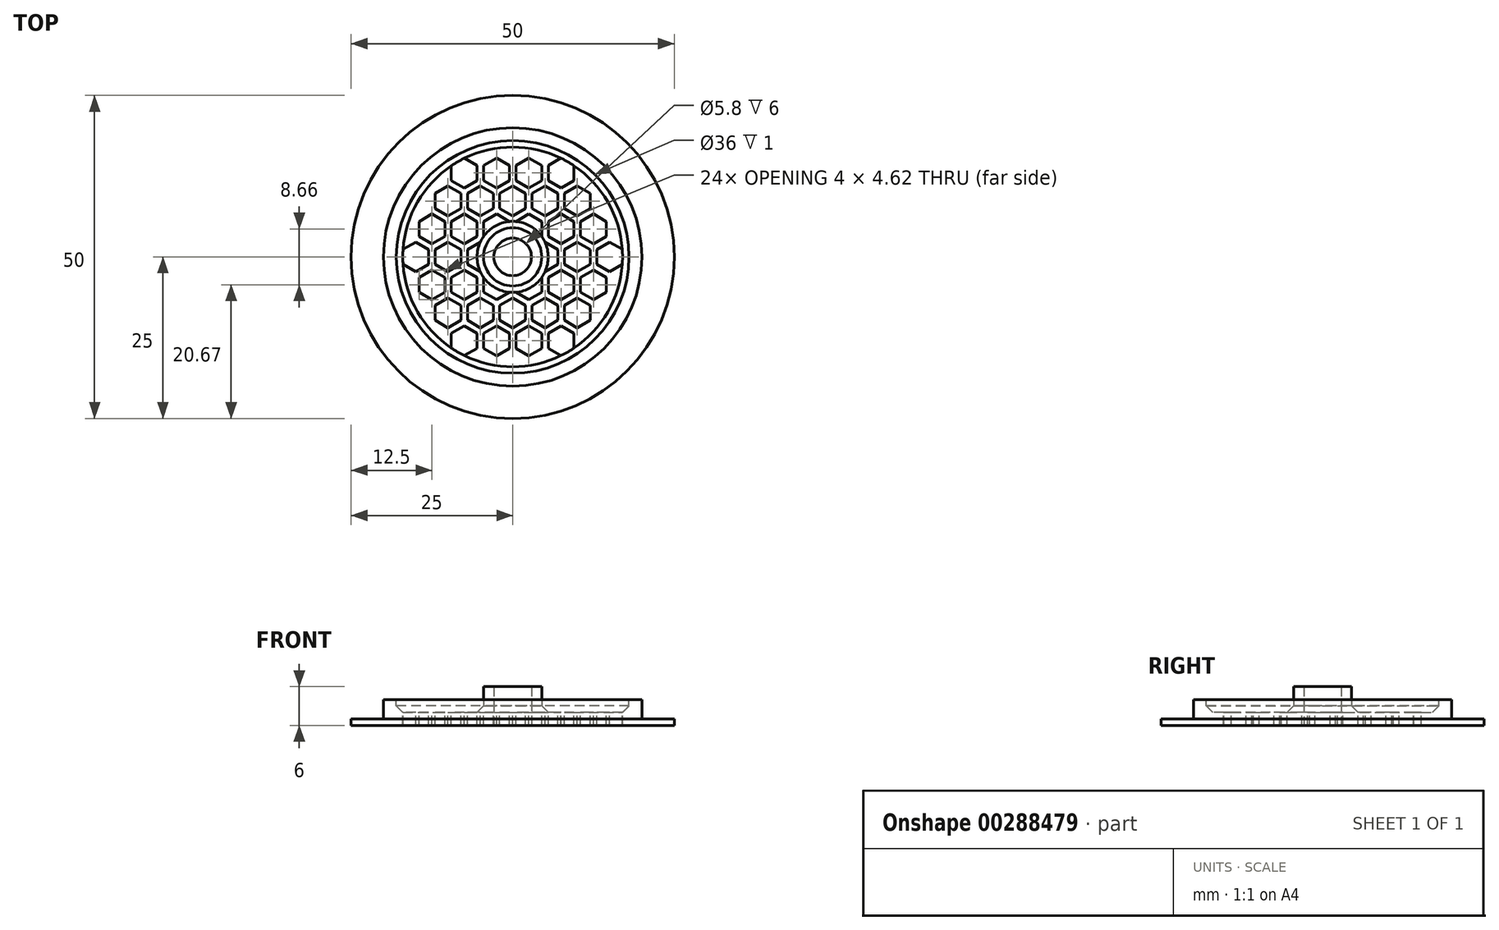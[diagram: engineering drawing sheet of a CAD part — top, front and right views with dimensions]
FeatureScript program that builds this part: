
annotation { "Feature Type Name" : "Feature", "Feature Type Description" : "" }
export const myFeature = defineFeature(function(context is Context, id is Id, definition is map)
    precondition{}
    {
        {
            var Q0;
            Q0=qCreatedBy(makeId("Top.planeOp"),FACE);
            var sketch = newSketch(context, id + "F0", { "sketchPlane" : qUnion([Q0])});
            skCircle(sketch, "E0", {"center": v(0, 0) * mm, "radius": 25 * mm});
            skCircle(sketch, "E1", {"center": v(0, 0) * mm, "radius": 20 * mm});
            skCircle(sketch, "E2", {"center": v(0, 0) * mm, "radius": 2.9 * mm});
            skSolve(sketch);
        }
        {
            var Q0;
            Q0=makeQuery(id+"F0.imprint","IMPRINT",FACE,{"disambiguationData":[TD([[makeQuery(id+"F0.imprint","IMPRINT",EDGE,{"derivedFrom":sQuery(id+"F0.wireOp",EDGE,"E1")}),1.0]])]});
            var Q1;
            Q1=makeQuery(id+"F0.imprint","IMPRINT",FACE,{"disambiguationData":[TD([[makeQuery(id+"F0.imprint","IMPRINT",EDGE,{"derivedFrom":sQuery(id+"F0.wireOp",EDGE,"E0")}),1.0]])]});
            extrude(context, id + "F1", {"entities" : qUnion([Q0, Q1]), "depth" : 1 * mm});
        }
        {
            var Q0;
            Q0=makeQuery(id+"F0.imprint","IMPRINT",FACE,{"disambiguationData":[TD([[makeQuery(id+"F0.imprint","IMPRINT",EDGE,{"derivedFrom":sQuery(id+"F0.wireOp",EDGE,"E1")}),1.0]])]});
            extrude(context, id + "F2", {"entities" : qUnion([Q0]), "operationType" : NewBodyOperationType.ADD, "depth" : 4 * mm});
        }
        {
            var Q0;
            Q0=makeQuery(id+"F2.opExtrude","CAP_FACE",FACE,{"disambiguationData":[OSD([sQuery(id+"F0.wireOp",EDGE,"E1"),sQuery(id+"F0.wireOp",EDGE,"E2")])],"isStart":false});
            var sketch = newSketch(context, id + "F3", { "sketchPlane" : qUnion([Q0])});
            skCircle(sketch, "E3", {"center": v(0, 0) * mm, "radius": 4.5 * mm});
            skCircle(sketch, "E4.0", {"center": v(0, 0) * mm, "radius": 18 * mm});
            skSolve(sketch);
        }
        {
            var Q0;
            Q0=makeQuery(id+"F3.imprint","IMPRINT",FACE,{"disambiguationData":[TD([[makeQuery(id+"F3.imprint","IMPRINT",EDGE,{"derivedFrom":sQuery(id+"F3.wireOp",EDGE,"E3")}),1.0]])]});
            extrude(context, id + "F4", {"entities" : qUnion([Q0]), "operationType" : NewBodyOperationType.ADD, "depth" : 2 * mm});
        }
        {
            var Q0;
            Q0=makeQuery(id+"F3.imprint","IMPRINT",FACE,{"disambiguationData":[TD([[makeQuery(id+"F3.imprint","IMPRINT",EDGE,{"derivedFrom":sQuery(id+"F3.wireOp",EDGE,"E3")}),-1.0]])]});
            extrude(context, id + "F5", {"entities" : qUnion([Q0]), "operationType" : NewBodyOperationType.REMOVE, "oppositeDirection" : true, "depth" : 2 * mm});
        }
        {
            var Q0;
            Q0=makeQuery(id+"F5.boolean.opBoolean","COPY",FACE,{"derivedFrom":makeQuery(id+"F5.opExtrude","CAP_FACE",FACE,{"disambiguationData":[OSD([sQuery(id+"F3.wireOp",EDGE,"E3"),sQuery(id+"F3.wireOp",EDGE,"E4.0")])],"isStart":false})});
            chamfer(context, id + "F6", {"entities" : qUnion([Q0]), "width" : 1 * mm, "tangentPropagation" : true});
        }
        {
            var Q0;
            Q0=makeQuery(id+"F5.boolean.opBoolean","COPY",FACE,{"derivedFrom":makeQuery(id+"F5.opExtrude","CAP_FACE",FACE,{"disambiguationData":[OSD([sQuery(id+"F3.wireOp",EDGE,"E3"),sQuery(id+"F3.wireOp",EDGE,"E4.0")])],"isStart":false})});
            var sketch = newSketch(context, id + "F7", { "sketchPlane" : qUnion([Q0])});
            skLineSegment(sketch, "E5.bottom", {"start": v(-17, 17) * mm, "end": v(17, 17) * mm, "construction": true});
            skLineSegment(sketch, "E5.top", {"start": v(-17, -17) * mm, "end": v(17, -17) * mm, "construction": true});
            skLineSegment(sketch, "E5.left", {"start": v(-17, 17) * mm, "end": v(-17, -17) * mm, "construction": true});
            skLineSegment(sketch, "E5.right", {"start": v(17, 17) * mm, "end": v(17, -17) * mm, "construction": true});
            skPoint(sketch, "E5.middle", {"position": v(0, 0) * mm});
            skCircle(sketch, "E6.cCircle", {"center": v(-2.5, -4.33) * mm, "radius": 2 * mm, "construction": true});
            skLineSegment(sketch, "E6.0", {"start": v(-0.5, -3.18) * mm, "end": v(-0.5, -5.48) * mm});
            skLineSegment(sketch, "E6.1", {"start": v(-0.5, -5.48) * mm, "end": v(-2.5, -6.64) * mm});
            skLineSegment(sketch, "E6.2", {"start": v(-2.5, -6.64) * mm, "end": v(-4.5, -5.48) * mm});
            skLineSegment(sketch, "E6.3", {"start": v(-4.5, -5.48) * mm, "end": v(-4.5, -3.18) * mm});
            skLineSegment(sketch, "E6.4", {"start": v(-4.5, -3.18) * mm, "end": v(-2.5, -2.02) * mm});
            skLineSegment(sketch, "E6.5", {"start": v(-2.5, -2.02) * mm, "end": v(-0.5, -3.18) * mm});
            skPoint(sketch, "E6.0.midPoint", {"position": v(-0.5, -4.33) * mm});
            skCircle(sketch, "E7.cCircle", {"center": v(-2.5, -4.33) * mm, "radius": 2.5 * mm, "construction": true});
            skLineSegment(sketch, "E7.0", {"start": v(0, -2.89) * mm, "end": v(0, -5.77) * mm, "construction": true});
            skLineSegment(sketch, "E7.1", {"start": v(0, -5.77) * mm, "end": v(-2.5, -7.22) * mm, "construction": true});
            skLineSegment(sketch, "E7.2", {"start": v(-2.5, -7.22) * mm, "end": v(-5, -5.77) * mm, "construction": true});
            skLineSegment(sketch, "E7.3", {"start": v(-5, -5.77) * mm, "end": v(-5, -2.89) * mm, "construction": true});
            skLineSegment(sketch, "E7.4", {"start": v(-5, -2.89) * mm, "end": v(-2.5, -1.44) * mm, "construction": true});
            skLineSegment(sketch, "E7.5", {"start": v(-2.5, -1.44) * mm, "end": v(0, -2.89) * mm, "construction": true});
            skPoint(sketch, "E7.0.midPoint", {"position": v(0, -4.33) * mm});
            skPoint(sketch, "E8.1.0", {"position": v(3.75, -2.17) * mm});
            skPoint(sketch, "E8.1.1", {"position": v(3.5, -2.6) * mm});
            skLineSegment(sketch, "E8.1.2", {"start": v(0, -2.89) * mm, "end": v(2.5, -1.44) * mm, "construction": true});
            skLineSegment(sketch, "E8.1.3", {"start": v(2.5, -1.44) * mm, "end": v(5, -2.89) * mm, "construction": true});
            skLineSegment(sketch, "E8.1.4", {"start": v(0.5, -3.18) * mm, "end": v(2.5, -2.02) * mm});
            skLineSegment(sketch, "E8.1.5", {"start": v(0.5, -5.48) * mm, "end": v(0.5, -3.18) * mm});
            skLineSegment(sketch, "E8.1.6", {"start": v(2.5, -6.64) * mm, "end": v(0.5, -5.48) * mm});
            skLineSegment(sketch, "E8.1.7", {"start": v(4.5, -5.48) * mm, "end": v(2.5, -6.64) * mm});
            skLineSegment(sketch, "E8.1.8", {"start": v(2.5, -7.22) * mm, "end": v(0, -5.77) * mm, "construction": true});
            skLineSegment(sketch, "E8.1.9", {"start": v(5, -5.77) * mm, "end": v(2.5, -7.22) * mm, "construction": true});
            skLineSegment(sketch, "E8.1.10", {"start": v(5, -2.89) * mm, "end": v(5, -5.77) * mm, "construction": true});
            skLineSegment(sketch, "E8.1.11", {"start": v(0, -5.77) * mm, "end": v(0, -2.89) * mm, "construction": true});
            skLineSegment(sketch, "E8.1.12", {"start": v(4.5, -3.18) * mm, "end": v(4.5, -5.48) * mm});
            skLineSegment(sketch, "E8.1.13", {"start": v(2.5, -2.02) * mm, "end": v(4.5, -3.18) * mm});
            skPoint(sketch, "E8.2.0", {"position": v(3.75, 2.17) * mm});
            skPoint(sketch, "E8.2.1", {"position": v(4, 1.73) * mm});
            skLineSegment(sketch, "E8.2.2", {"start": v(2.5, -1.44) * mm, "end": v(2.5, 1.44) * mm, "construction": true});
            skLineSegment(sketch, "E8.2.3", {"start": v(2.5, 1.44) * mm, "end": v(5, 2.89) * mm, "construction": true});
            skLineSegment(sketch, "E8.2.4", {"start": v(3, -1.15) * mm, "end": v(3, 1.15) * mm});
            skLineSegment(sketch, "E8.2.5", {"start": v(5, -2.3) * mm, "end": v(3, -1.15) * mm});
            skLineSegment(sketch, "E8.2.6", {"start": v(7, -1.15) * mm, "end": v(5, -2.3) * mm});
            skLineSegment(sketch, "E8.2.7", {"start": v(7, 1.15) * mm, "end": v(7, -1.15) * mm});
            skLineSegment(sketch, "E8.2.8", {"start": v(7.5, -1.44) * mm, "end": v(5, -2.89) * mm, "construction": true});
            skLineSegment(sketch, "E8.2.9", {"start": v(7.5, 1.44) * mm, "end": v(7.5, -1.44) * mm, "construction": true});
            skLineSegment(sketch, "E8.2.10", {"start": v(5, 2.89) * mm, "end": v(7.5, 1.44) * mm, "construction": true});
            skLineSegment(sketch, "E8.2.11", {"start": v(5, -2.89) * mm, "end": v(2.5, -1.44) * mm, "construction": true});
            skLineSegment(sketch, "E8.2.12", {"start": v(5, 2.3) * mm, "end": v(7, 1.15) * mm});
            skLineSegment(sketch, "E8.2.13", {"start": v(3, 1.15) * mm, "end": v(5, 2.3) * mm});
            skPoint(sketch, "E8.3.0", {"position": v(0, 4.33) * mm});
            skPoint(sketch, "E8.3.1", {"position": v(0.5, 4.33) * mm});
            skLineSegment(sketch, "E8.3.2", {"start": v(2.5, 1.44) * mm, "end": v(0, 2.89) * mm, "construction": true});
            skLineSegment(sketch, "E8.3.3", {"start": v(0, 2.89) * mm, "end": v(0, 5.77) * mm, "construction": true});
            skLineSegment(sketch, "E8.3.4", {"start": v(2.5, 2.02) * mm, "end": v(0.5, 3.18) * mm});
            skLineSegment(sketch, "E8.3.5", {"start": v(4.5, 3.18) * mm, "end": v(2.5, 2.02) * mm});
            skLineSegment(sketch, "E8.3.6", {"start": v(4.5, 5.48) * mm, "end": v(4.5, 3.18) * mm});
            skLineSegment(sketch, "E8.3.7", {"start": v(2.5, 6.64) * mm, "end": v(4.5, 5.48) * mm});
            skLineSegment(sketch, "E8.3.8", {"start": v(5, 5.77) * mm, "end": v(5, 2.89) * mm, "construction": true});
            skLineSegment(sketch, "E8.3.9", {"start": v(2.5, 7.22) * mm, "end": v(5, 5.77) * mm, "construction": true});
            skLineSegment(sketch, "E8.3.10", {"start": v(0, 5.77) * mm, "end": v(2.5, 7.22) * mm, "construction": true});
            skLineSegment(sketch, "E8.3.11", {"start": v(5, 2.89) * mm, "end": v(2.5, 1.44) * mm, "construction": true});
            skLineSegment(sketch, "E8.3.12", {"start": v(0.5, 5.48) * mm, "end": v(2.5, 6.64) * mm});
            skLineSegment(sketch, "E8.3.13", {"start": v(0.5, 3.18) * mm, "end": v(0.5, 5.48) * mm});
            skPoint(sketch, "E8.4.0", {"position": v(-3.75, 2.17) * mm});
            skPoint(sketch, "E8.4.1", {"position": v(-3.5, 2.6) * mm});
            skLineSegment(sketch, "E8.4.2", {"start": v(0, 2.89) * mm, "end": v(-2.5, 1.44) * mm, "construction": true});
            skLineSegment(sketch, "E8.4.3", {"start": v(-2.5, 1.44) * mm, "end": v(-5, 2.89) * mm, "construction": true});
            skLineSegment(sketch, "E8.4.4", {"start": v(-0.5, 3.18) * mm, "end": v(-2.5, 2.02) * mm});
            skLineSegment(sketch, "E8.4.5", {"start": v(-0.5, 5.48) * mm, "end": v(-0.5, 3.18) * mm});
            skLineSegment(sketch, "E8.4.6", {"start": v(-2.5, 6.64) * mm, "end": v(-0.5, 5.48) * mm});
            skLineSegment(sketch, "E8.4.7", {"start": v(-4.5, 5.48) * mm, "end": v(-2.5, 6.64) * mm});
            skLineSegment(sketch, "E8.4.8", {"start": v(-2.5, 7.22) * mm, "end": v(0, 5.77) * mm, "construction": true});
            skLineSegment(sketch, "E8.4.9", {"start": v(-5, 5.77) * mm, "end": v(-2.5, 7.22) * mm, "construction": true});
            skLineSegment(sketch, "E8.4.10", {"start": v(-5, 2.89) * mm, "end": v(-5, 5.77) * mm, "construction": true});
            skLineSegment(sketch, "E8.4.11", {"start": v(0, 5.77) * mm, "end": v(0, 2.89) * mm, "construction": true});
            skLineSegment(sketch, "E8.4.12", {"start": v(-4.5, 3.18) * mm, "end": v(-4.5, 5.48) * mm});
            skLineSegment(sketch, "E8.4.13", {"start": v(-2.5, 2.02) * mm, "end": v(-4.5, 3.18) * mm});
            skPoint(sketch, "E8.5.0", {"position": v(-3.75, -2.17) * mm});
            skPoint(sketch, "E8.5.1", {"position": v(-4, -1.73) * mm});
            skLineSegment(sketch, "E8.5.2", {"start": v(-2.5, 1.44) * mm, "end": v(-2.5, -1.44) * mm, "construction": true});
            skLineSegment(sketch, "E8.5.3", {"start": v(-2.5, -1.44) * mm, "end": v(-5, -2.89) * mm, "construction": true});
            skLineSegment(sketch, "E8.5.4", {"start": v(-3, 1.15) * mm, "end": v(-3, -1.15) * mm});
            skLineSegment(sketch, "E8.5.5", {"start": v(-5, 2.3) * mm, "end": v(-3, 1.15) * mm});
            skLineSegment(sketch, "E8.5.6", {"start": v(-7, 1.15) * mm, "end": v(-5, 2.3) * mm});
            skLineSegment(sketch, "E8.5.7", {"start": v(-7, -1.15) * mm, "end": v(-7, 1.15) * mm});
            skLineSegment(sketch, "E8.5.8", {"start": v(-7.5, 1.44) * mm, "end": v(-5, 2.89) * mm, "construction": true});
            skLineSegment(sketch, "E8.5.9", {"start": v(-7.5, -1.44) * mm, "end": v(-7.5, 1.44) * mm, "construction": true});
            skLineSegment(sketch, "E8.5.10", {"start": v(-5, -2.89) * mm, "end": v(-7.5, -1.44) * mm, "construction": true});
            skLineSegment(sketch, "E8.5.11", {"start": v(-5, 2.89) * mm, "end": v(-2.5, 1.44) * mm, "construction": true});
            skLineSegment(sketch, "E8.5.12", {"start": v(-5, -2.3) * mm, "end": v(-7, -1.15) * mm});
            skLineSegment(sketch, "E8.5.13", {"start": v(-3, -1.15) * mm, "end": v(-5, -2.3) * mm});
            skLineSegment(sketch, "E9", {"start": v(-2.5, -1.44) * mm, "end": v(0, 0) * mm, "construction": true});
            skLineSegment(sketch, "E10", {"start": v(0, 0) * mm, "end": v(0, -2.89) * mm, "construction": true});
            skLineSegment(sketch, "E11.MirrorCS", {"start": v(-2, 1.15) * mm, "end": v(-2, -1.15) * mm});
            skLineSegment(sketch, "E12.MirrorCS", {"start": v(-2, -1.15) * mm, "end": v(0, -2.3) * mm});
            skLineSegment(sketch, "E13.MirrorCS", {"start": v(0, -2.3) * mm, "end": v(2, -1.15) * mm});
            skLineSegment(sketch, "E14.MirrorCS", {"start": v(2, -1.15) * mm, "end": v(2, 1.15) * mm});
            skLineSegment(sketch, "E15.MirrorCS", {"start": v(2, 1.15) * mm, "end": v(0, 2.3) * mm});
            skLineSegment(sketch, "E16.MirrorCS", {"start": v(0, 2.3) * mm, "end": v(-2, 1.15) * mm});
            skLineSegment(sketch, "E17.MirrorCS", {"start": v(2, -7.5) * mm, "end": v(0, -6.35) * mm});
            skLineSegment(sketch, "E18.MirrorCS", {"start": v(0, -6.35) * mm, "end": v(-2, -7.5) * mm});
            skLineSegment(sketch, "E19.MirrorCS", {"start": v(-2, -7.5) * mm, "end": v(-2, -9.81) * mm});
            skLineSegment(sketch, "E20.MirrorCS", {"start": v(-2, -9.81) * mm, "end": v(0, -10.97) * mm});
            skLineSegment(sketch, "E21.MirrorCS", {"start": v(0, -10.97) * mm, "end": v(2, -9.81) * mm});
            skLineSegment(sketch, "E22.MirrorCS", {"start": v(2, -9.81) * mm, "end": v(2, -7.5) * mm});
            skLineSegment(sketch, "E23.1.0", {"start": v(5.5, -3.18) * mm, "end": v(5.5, -5.48) * mm});
            skLineSegment(sketch, "E23.1.1", {"start": v(5.5, -5.48) * mm, "end": v(7.5, -6.64) * mm});
            skLineSegment(sketch, "E23.1.2", {"start": v(7.5, -6.64) * mm, "end": v(9.5, -5.48) * mm});
            skLineSegment(sketch, "E23.1.3", {"start": v(9.5, -5.48) * mm, "end": v(9.5, -3.18) * mm});
            skLineSegment(sketch, "E23.1.4", {"start": v(9.5, -3.18) * mm, "end": v(7.5, -2.02) * mm});
            skLineSegment(sketch, "E23.1.5", {"start": v(7.5, -2.02) * mm, "end": v(5.5, -3.18) * mm});
            skLineSegment(sketch, "E23.2.0", {"start": v(5.5, 3.18) * mm, "end": v(7.5, 2.02) * mm});
            skLineSegment(sketch, "E23.2.1", {"start": v(7.5, 2.02) * mm, "end": v(9.5, 3.18) * mm});
            skLineSegment(sketch, "E23.2.2", {"start": v(9.5, 3.18) * mm, "end": v(9.5, 5.48) * mm});
            skLineSegment(sketch, "E23.2.3", {"start": v(9.5, 5.48) * mm, "end": v(7.5, 6.64) * mm});
            skLineSegment(sketch, "E23.2.4", {"start": v(7.5, 6.64) * mm, "end": v(5.5, 5.48) * mm});
            skLineSegment(sketch, "E23.2.5", {"start": v(5.5, 5.48) * mm, "end": v(5.5, 3.18) * mm});
            skLineSegment(sketch, "E23.3.0", {"start": v(0, 6.35) * mm, "end": v(2, 7.5) * mm});
            skLineSegment(sketch, "E23.3.1", {"start": v(2, 7.5) * mm, "end": v(2, 9.81) * mm});
            skLineSegment(sketch, "E23.3.2", {"start": v(2, 9.81) * mm, "end": v(0, 10.97) * mm});
            skLineSegment(sketch, "E23.3.3", {"start": v(0, 10.97) * mm, "end": v(-2, 9.81) * mm});
            skLineSegment(sketch, "E23.3.4", {"start": v(-2, 9.81) * mm, "end": v(-2, 7.5) * mm});
            skLineSegment(sketch, "E23.3.5", {"start": v(-2, 7.5) * mm, "end": v(0, 6.35) * mm});
            skLineSegment(sketch, "E23.4.0", {"start": v(-5.5, 3.18) * mm, "end": v(-5.5, 5.48) * mm});
            skLineSegment(sketch, "E23.4.1", {"start": v(-5.5, 5.48) * mm, "end": v(-7.5, 6.64) * mm});
            skLineSegment(sketch, "E23.4.2", {"start": v(-7.5, 6.64) * mm, "end": v(-9.5, 5.48) * mm});
            skLineSegment(sketch, "E23.4.3", {"start": v(-9.5, 5.48) * mm, "end": v(-9.5, 3.18) * mm});
            skLineSegment(sketch, "E23.4.4", {"start": v(-9.5, 3.18) * mm, "end": v(-7.5, 2.02) * mm});
            skLineSegment(sketch, "E23.4.5", {"start": v(-7.5, 2.02) * mm, "end": v(-5.5, 3.18) * mm});
            skLineSegment(sketch, "E23.5.0", {"start": v(-5.5, -3.18) * mm, "end": v(-7.5, -2.02) * mm});
            skLineSegment(sketch, "E23.5.1", {"start": v(-7.5, -2.02) * mm, "end": v(-9.5, -3.18) * mm});
            skLineSegment(sketch, "E23.5.2", {"start": v(-9.5, -3.18) * mm, "end": v(-9.5, -5.48) * mm});
            skLineSegment(sketch, "E23.5.3", {"start": v(-9.5, -5.48) * mm, "end": v(-7.5, -6.64) * mm});
            skLineSegment(sketch, "E23.5.4", {"start": v(-7.5, -6.64) * mm, "end": v(-5.5, -5.48) * mm});
            skLineSegment(sketch, "E23.5.5", {"start": v(-5.5, -5.48) * mm, "end": v(-5.5, -3.18) * mm});
            skLineSegment(sketch, "E24.MirrorCS", {"start": v(5, -6.35) * mm, "end": v(3, -7.5) * mm});
            skLineSegment(sketch, "E25.MirrorCS", {"start": v(3, -7.5) * mm, "end": v(3, -9.81) * mm});
            skLineSegment(sketch, "E26.MirrorCS", {"start": v(3, -9.81) * mm, "end": v(5, -10.97) * mm});
            skLineSegment(sketch, "E27.MirrorCS", {"start": v(5, -10.97) * mm, "end": v(7, -9.81) * mm});
            skLineSegment(sketch, "E28.MirrorCS", {"start": v(7, -9.81) * mm, "end": v(7, -7.5) * mm});
            skLineSegment(sketch, "E29.MirrorCS", {"start": v(7, -7.5) * mm, "end": v(5, -6.35) * mm});
            skLineSegment(sketch, "E30.1.0", {"start": v(8, 1.15) * mm, "end": v(8, -1.15) * mm});
            skLineSegment(sketch, "E30.1.1", {"start": v(10, 2.3) * mm, "end": v(8, 1.15) * mm});
            skLineSegment(sketch, "E30.1.2", {"start": v(12, 1.15) * mm, "end": v(10, 2.3) * mm});
            skLineSegment(sketch, "E30.1.3", {"start": v(12, -1.15) * mm, "end": v(12, 1.15) * mm});
            skLineSegment(sketch, "E30.1.4", {"start": v(10, -2.3) * mm, "end": v(12, -1.15) * mm});
            skLineSegment(sketch, "E30.1.5", {"start": v(8, -1.15) * mm, "end": v(10, -2.3) * mm});
            skLineSegment(sketch, "E30.2.0", {"start": v(3, 7.5) * mm, "end": v(5, 6.35) * mm});
            skLineSegment(sketch, "E30.2.1", {"start": v(3, 9.81) * mm, "end": v(3, 7.5) * mm});
            skLineSegment(sketch, "E30.2.2", {"start": v(5, 10.97) * mm, "end": v(3, 9.81) * mm});
            skLineSegment(sketch, "E30.2.3", {"start": v(7, 9.81) * mm, "end": v(5, 10.97) * mm});
            skLineSegment(sketch, "E30.2.4", {"start": v(7, 7.5) * mm, "end": v(7, 9.81) * mm});
            skLineSegment(sketch, "E30.2.5", {"start": v(5, 6.35) * mm, "end": v(7, 7.5) * mm});
            skLineSegment(sketch, "E30.3.0", {"start": v(-5, 6.35) * mm, "end": v(-3, 7.5) * mm});
            skLineSegment(sketch, "E30.3.1", {"start": v(-7, 7.5) * mm, "end": v(-5, 6.35) * mm});
            skLineSegment(sketch, "E30.3.2", {"start": v(-7, 9.81) * mm, "end": v(-7, 7.5) * mm});
            skLineSegment(sketch, "E30.3.3", {"start": v(-5, 10.97) * mm, "end": v(-7, 9.81) * mm});
            skLineSegment(sketch, "E30.3.4", {"start": v(-3, 9.81) * mm, "end": v(-5, 10.97) * mm});
            skLineSegment(sketch, "E30.3.5", {"start": v(-3, 7.5) * mm, "end": v(-3, 9.81) * mm});
            skLineSegment(sketch, "E30.4.0", {"start": v(-8, -1.15) * mm, "end": v(-8, 1.15) * mm});
            skLineSegment(sketch, "E30.4.1", {"start": v(-10, -2.3) * mm, "end": v(-8, -1.15) * mm});
            skLineSegment(sketch, "E30.4.2", {"start": v(-12, -1.15) * mm, "end": v(-10, -2.3) * mm});
            skLineSegment(sketch, "E30.4.3", {"start": v(-12, 1.15) * mm, "end": v(-12, -1.15) * mm});
            skLineSegment(sketch, "E30.4.4", {"start": v(-10, 2.3) * mm, "end": v(-12, 1.15) * mm});
            skLineSegment(sketch, "E30.4.5", {"start": v(-8, 1.15) * mm, "end": v(-10, 2.3) * mm});
            skLineSegment(sketch, "E30.5.0", {"start": v(-3, -7.5) * mm, "end": v(-5, -6.35) * mm});
            skLineSegment(sketch, "E30.5.1", {"start": v(-3, -9.81) * mm, "end": v(-3, -7.5) * mm});
            skLineSegment(sketch, "E30.5.2", {"start": v(-5, -10.97) * mm, "end": v(-3, -9.81) * mm});
            skLineSegment(sketch, "E30.5.3", {"start": v(-7, -9.81) * mm, "end": v(-5, -10.97) * mm});
            skLineSegment(sketch, "E30.5.4", {"start": v(-7, -7.5) * mm, "end": v(-7, -9.81) * mm});
            skLineSegment(sketch, "E30.5.5", {"start": v(-5, -6.35) * mm, "end": v(-7, -7.5) * mm});
            skLineSegment(sketch, "E31.MirrorCS", {"start": v(-5.5, 11.84) * mm, "end": v(-7.5, 10.68) * mm});
            skLineSegment(sketch, "E32.MirrorCS", {"start": v(-5.5, 14.15) * mm, "end": v(-5.5, 11.84) * mm});
            skLineSegment(sketch, "E33.MirrorCS", {"start": v(-7.5, 15.3) * mm, "end": v(-5.5, 14.15) * mm});
            skLineSegment(sketch, "E34.MirrorCS", {"start": v(-9.5, 14.15) * mm, "end": v(-7.5, 15.3) * mm});
            skLineSegment(sketch, "E35.MirrorCS", {"start": v(-9.5, 11.84) * mm, "end": v(-9.5, 14.15) * mm});
            skLineSegment(sketch, "E36.MirrorCS", {"start": v(-7.5, 10.68) * mm, "end": v(-9.5, 11.84) * mm});
            skLineSegment(sketch, "E37.MirrorCS", {"start": v(-2.5, 10.68) * mm, "end": v(-0.5, 11.84) * mm});
            skLineSegment(sketch, "E38.MirrorCS", {"start": v(-0.5, 11.84) * mm, "end": v(-0.5, 14.15) * mm});
            skLineSegment(sketch, "E39.MirrorCS", {"start": v(-0.5, 14.15) * mm, "end": v(-2.5, 15.3) * mm});
            skLineSegment(sketch, "E40.MirrorCS", {"start": v(-2.5, 15.3) * mm, "end": v(-4.5, 14.15) * mm});
            skLineSegment(sketch, "E41.MirrorCS", {"start": v(-4.5, 14.15) * mm, "end": v(-4.5, 11.84) * mm});
            skLineSegment(sketch, "E42.MirrorCS", {"start": v(-4.5, 11.84) * mm, "end": v(-2.5, 10.68) * mm});
            skLineSegment(sketch, "E43.MirrorCS", {"start": v(0.5, 11.84) * mm, "end": v(2.5, 10.68) * mm});
            skLineSegment(sketch, "E44.MirrorCS", {"start": v(0.5, 14.15) * mm, "end": v(0.5, 11.84) * mm});
            skLineSegment(sketch, "E45.MirrorCS", {"start": v(2.5, 15.3) * mm, "end": v(0.5, 14.15) * mm});
            skLineSegment(sketch, "E46.MirrorCS", {"start": v(4.5, 14.15) * mm, "end": v(2.5, 15.3) * mm});
            skLineSegment(sketch, "E47.MirrorCS", {"start": v(4.5, 11.84) * mm, "end": v(4.5, 14.15) * mm});
            skLineSegment(sketch, "E48.MirrorCS", {"start": v(2.5, 10.68) * mm, "end": v(4.5, 11.84) * mm});
            skLineSegment(sketch, "E49.MirrorCS", {"start": v(7.5, 10.68) * mm, "end": v(5.5, 11.84) * mm});
            skLineSegment(sketch, "E50.MirrorCS", {"start": v(5.5, 11.84) * mm, "end": v(5.5, 14.15) * mm});
            skLineSegment(sketch, "E51.MirrorCS", {"start": v(5.5, 14.15) * mm, "end": v(7.5, 15.3) * mm});
            skLineSegment(sketch, "E52.MirrorCS", {"start": v(7.5, 15.3) * mm, "end": v(9.5, 14.15) * mm});
            skLineSegment(sketch, "E53.MirrorCS", {"start": v(9.5, 14.15) * mm, "end": v(9.5, 11.84) * mm});
            skLineSegment(sketch, "E54.MirrorCS", {"start": v(9.5, 11.84) * mm, "end": v(7.5, 10.68) * mm});
            skLineSegment(sketch, "E55.MirrorCS", {"start": v(8, 7.5) * mm, "end": v(10, 6.35) * mm});
            skLineSegment(sketch, "E56.MirrorCS", {"start": v(8, 9.81) * mm, "end": v(8, 7.5) * mm});
            skLineSegment(sketch, "E57.MirrorCS", {"start": v(10, 10.97) * mm, "end": v(8, 9.81) * mm});
            skLineSegment(sketch, "E58.MirrorCS", {"start": v(12, 9.81) * mm, "end": v(10, 10.97) * mm});
            skLineSegment(sketch, "E59.MirrorCS", {"start": v(12, 7.5) * mm, "end": v(12, 9.81) * mm});
            skLineSegment(sketch, "E60.MirrorCS", {"start": v(10, 6.35) * mm, "end": v(12, 7.5) * mm});
            skLineSegment(sketch, "E61.MirrorCS", {"start": v(10.5, 5.48) * mm, "end": v(10.5, 3.18) * mm});
            skLineSegment(sketch, "E62.MirrorCS", {"start": v(12.5, 6.64) * mm, "end": v(10.5, 5.48) * mm});
            skLineSegment(sketch, "E63.MirrorCS", {"start": v(14.5, 5.48) * mm, "end": v(12.5, 6.64) * mm});
            skLineSegment(sketch, "E64.MirrorCS", {"start": v(14.5, 3.18) * mm, "end": v(14.5, 5.48) * mm});
            skLineSegment(sketch, "E65.MirrorCS", {"start": v(12.5, 2.02) * mm, "end": v(14.5, 3.18) * mm});
            skLineSegment(sketch, "E66.MirrorCS", {"start": v(10.5, 3.18) * mm, "end": v(12.5, 2.02) * mm});
            skLineSegment(sketch, "E67.MirrorCS", {"start": v(10.5, -3.18) * mm, "end": v(10.5, -5.48) * mm});
            skLineSegment(sketch, "E68.MirrorCS", {"start": v(12.5, -2.02) * mm, "end": v(10.5, -3.18) * mm});
            skLineSegment(sketch, "E69.MirrorCS", {"start": v(14.5, -3.18) * mm, "end": v(12.5, -2.02) * mm});
            skLineSegment(sketch, "E70.MirrorCS", {"start": v(14.5, -5.48) * mm, "end": v(14.5, -3.18) * mm});
            skLineSegment(sketch, "E71.MirrorCS", {"start": v(12.5, -6.64) * mm, "end": v(14.5, -5.48) * mm});
            skLineSegment(sketch, "E72.MirrorCS", {"start": v(10.5, -5.48) * mm, "end": v(12.5, -6.64) * mm});
            skLineSegment(sketch, "E73.MirrorCS", {"start": v(10, -6.35) * mm, "end": v(8, -7.5) * mm});
            skLineSegment(sketch, "E74.MirrorCS", {"start": v(12, -7.5) * mm, "end": v(10, -6.35) * mm});
            skLineSegment(sketch, "E75.MirrorCS", {"start": v(12, -9.81) * mm, "end": v(12, -7.5) * mm});
            skLineSegment(sketch, "E76.MirrorCS", {"start": v(10, -10.97) * mm, "end": v(12, -9.81) * mm});
            skLineSegment(sketch, "E77.MirrorCS", {"start": v(8, -9.81) * mm, "end": v(10, -10.97) * mm});
            skLineSegment(sketch, "E78.MirrorCS", {"start": v(8, -7.5) * mm, "end": v(8, -9.81) * mm});
            skLineSegment(sketch, "E79.MirrorCS", {"start": v(5.5, -11.84) * mm, "end": v(7.5, -10.68) * mm});
            skLineSegment(sketch, "E80.MirrorCS", {"start": v(7.5, -10.68) * mm, "end": v(9.5, -11.84) * mm});
            skLineSegment(sketch, "E81.MirrorCS", {"start": v(9.5, -11.84) * mm, "end": v(9.5, -14.15) * mm});
            skLineSegment(sketch, "E82.MirrorCS", {"start": v(9.5, -14.15) * mm, "end": v(7.5, -15.3) * mm});
            skLineSegment(sketch, "E83.MirrorCS", {"start": v(7.5, -15.3) * mm, "end": v(5.5, -14.15) * mm});
            skLineSegment(sketch, "E84.MirrorCS", {"start": v(5.5, -14.15) * mm, "end": v(5.5, -11.84) * mm});
            skLineSegment(sketch, "E85.MirrorCS", {"start": v(2.5, -10.68) * mm, "end": v(0.5, -11.84) * mm});
            skLineSegment(sketch, "E86.MirrorCS", {"start": v(4.5, -11.84) * mm, "end": v(2.5, -10.68) * mm});
            skLineSegment(sketch, "E87.MirrorCS", {"start": v(4.5, -14.15) * mm, "end": v(4.5, -11.84) * mm});
            skLineSegment(sketch, "E88.MirrorCS", {"start": v(2.5, -15.3) * mm, "end": v(4.5, -14.15) * mm});
            skLineSegment(sketch, "E89.MirrorCS", {"start": v(0.5, -14.15) * mm, "end": v(2.5, -15.3) * mm});
            skLineSegment(sketch, "E90.MirrorCS", {"start": v(0.5, -11.84) * mm, "end": v(0.5, -14.15) * mm});
            skLineSegment(sketch, "E91.MirrorCS", {"start": v(-0.5, -11.84) * mm, "end": v(-2.5, -10.68) * mm});
            skLineSegment(sketch, "E92.MirrorCS", {"start": v(-0.5, -14.15) * mm, "end": v(-0.5, -11.84) * mm});
            skLineSegment(sketch, "E93.MirrorCS", {"start": v(-2.5, -15.3) * mm, "end": v(-0.5, -14.15) * mm});
            skLineSegment(sketch, "E94.MirrorCS", {"start": v(-5, -14.43) * mm, "end": v(-2.5, -15.88) * mm, "construction": true});
            skLineSegment(sketch, "E95.MirrorCS", {"start": v(-4.5, -14.15) * mm, "end": v(-2.5, -15.3) * mm});
            skLineSegment(sketch, "E96.MirrorCS", {"start": v(-4.5, -11.84) * mm, "end": v(-4.5, -14.15) * mm});
            skLineSegment(sketch, "E97.MirrorCS", {"start": v(-2.5, -10.68) * mm, "end": v(-4.5, -11.84) * mm});
            skLineSegment(sketch, "E98.MirrorCS", {"start": v(-7.5, -10.68) * mm, "end": v(-5.5, -11.84) * mm});
            skLineSegment(sketch, "E99.MirrorCS", {"start": v(-5.5, -11.84) * mm, "end": v(-5.5, -14.15) * mm});
            skLineSegment(sketch, "E100.MirrorCS", {"start": v(-5.5, -14.15) * mm, "end": v(-7.5, -15.3) * mm});
            skLineSegment(sketch, "E101.MirrorCS", {"start": v(-7.5, -15.3) * mm, "end": v(-9.5, -14.15) * mm});
            skLineSegment(sketch, "E102.MirrorCS", {"start": v(-9.5, -14.15) * mm, "end": v(-9.5, -11.84) * mm});
            skLineSegment(sketch, "E103.MirrorCS", {"start": v(-9.5, -11.84) * mm, "end": v(-7.5, -10.68) * mm});
            skLineSegment(sketch, "E104.MirrorCS", {"start": v(-8, -7.5) * mm, "end": v(-10, -6.35) * mm});
            skLineSegment(sketch, "E105.MirrorCS", {"start": v(-8, -9.81) * mm, "end": v(-8, -7.5) * mm});
            skLineSegment(sketch, "E106.MirrorCS", {"start": v(-10, -10.97) * mm, "end": v(-8, -9.81) * mm});
            skLineSegment(sketch, "E107.MirrorCS", {"start": v(-12, -9.81) * mm, "end": v(-10, -10.97) * mm});
            skLineSegment(sketch, "E108.MirrorCS", {"start": v(-12, -7.5) * mm, "end": v(-12, -9.81) * mm});
            skLineSegment(sketch, "E109.MirrorCS", {"start": v(-10, -6.35) * mm, "end": v(-12, -7.5) * mm});
            skLineSegment(sketch, "E110.MirrorCS", {"start": v(-12.5, -6.64) * mm, "end": v(-10.5, -5.48) * mm});
            skLineSegment(sketch, "E111.MirrorCS", {"start": v(-14.5, -5.48) * mm, "end": v(-12.5, -6.64) * mm});
            skLineSegment(sketch, "E112.MirrorCS", {"start": v(-14.5, -3.18) * mm, "end": v(-14.5, -5.48) * mm});
            skLineSegment(sketch, "E113.MirrorCS", {"start": v(-12.5, -2.02) * mm, "end": v(-14.5, -3.18) * mm});
            skLineSegment(sketch, "E114.MirrorCS", {"start": v(-10.5, -3.18) * mm, "end": v(-12.5, -2.02) * mm});
            skLineSegment(sketch, "E115.MirrorCS", {"start": v(-10.5, -5.48) * mm, "end": v(-10.5, -3.18) * mm});
            skLineSegment(sketch, "E116.MirrorCS", {"start": v(-10.5, 3.18) * mm, "end": v(-10.5, 5.48) * mm});
            skLineSegment(sketch, "E117.MirrorCS", {"start": v(-12.5, 2.02) * mm, "end": v(-10.5, 3.18) * mm});
            skLineSegment(sketch, "E118.MirrorCS", {"start": v(-14.5, 3.18) * mm, "end": v(-12.5, 2.02) * mm});
            skLineSegment(sketch, "E119.MirrorCS", {"start": v(-14.5, 5.48) * mm, "end": v(-14.5, 3.18) * mm});
            skLineSegment(sketch, "E120.MirrorCS", {"start": v(-12.5, 6.64) * mm, "end": v(-14.5, 5.48) * mm});
            skLineSegment(sketch, "E121.MirrorCS", {"start": v(-10.5, 5.48) * mm, "end": v(-12.5, 6.64) * mm});
            skLineSegment(sketch, "E122.MirrorCS", {"start": v(-10, 6.35) * mm, "end": v(-8, 7.5) * mm});
            skLineSegment(sketch, "E123.MirrorCS", {"start": v(-8, 7.5) * mm, "end": v(-8, 9.81) * mm});
            skLineSegment(sketch, "E124.MirrorCS", {"start": v(-8, 9.81) * mm, "end": v(-10, 10.97) * mm});
            skLineSegment(sketch, "E125.MirrorCS", {"start": v(-10, 10.97) * mm, "end": v(-12, 9.81) * mm});
            skLineSegment(sketch, "E126.MirrorCS", {"start": v(-12, 9.81) * mm, "end": v(-12, 7.5) * mm});
            skLineSegment(sketch, "E127.MirrorCS", {"start": v(-12, 7.5) * mm, "end": v(-10, 6.35) * mm});
            skLineSegment(sketch, "E128.MirrorCS", {"start": v(13, 1.15) * mm, "end": v(15, 2.3) * mm});
            skLineSegment(sketch, "E129.MirrorCS", {"start": v(15, 2.3) * mm, "end": v(17, 1.15) * mm});
            skLineSegment(sketch, "E130.MirrorCS", {"start": v(17, 1.15) * mm, "end": v(17, -1.15) * mm});
            skLineSegment(sketch, "E131.MirrorCS", {"start": v(17, -1.15) * mm, "end": v(15, -2.3) * mm});
            skLineSegment(sketch, "E132.MirrorCS", {"start": v(15, -2.3) * mm, "end": v(13, -1.15) * mm});
            skLineSegment(sketch, "E133.MirrorCS", {"start": v(13, -1.15) * mm, "end": v(13, 1.15) * mm});
            skLineSegment(sketch, "E134.MirrorCS", {"start": v(-15, 2.3) * mm, "end": v(-13, 1.15) * mm});
            skLineSegment(sketch, "E135.MirrorCS", {"start": v(-13, 1.15) * mm, "end": v(-13, -1.15) * mm});
            skLineSegment(sketch, "E136.MirrorCS", {"start": v(-13, -1.15) * mm, "end": v(-15, -2.3) * mm});
            skLineSegment(sketch, "E137.MirrorCS", {"start": v(-15, -2.3) * mm, "end": v(-17, -1.15) * mm});
            skLineSegment(sketch, "E138.MirrorCS", {"start": v(-17, -1.15) * mm, "end": v(-17, 1.15) * mm});
            skLineSegment(sketch, "E139.MirrorCS", {"start": v(-17, 1.15) * mm, "end": v(-15, 2.3) * mm});
            skSolve(sketch);
        }
        {
            var Q0;
            Q0=makeQuery(id+"F7.imprint","IMPRINT",FACE,{"disambiguationData":[TD([[makeQuery(id+"F7.imprint","IMPRINT",EDGE,{"derivedFrom":sQuery(id+"F7.wireOp",EDGE,"E31.MirrorCS")}),-1.0]])]});
            var Q1;
            Q1=makeQuery(id+"F7.imprint","IMPRINT",FACE,{"disambiguationData":[TD([[makeQuery(id+"F7.imprint","IMPRINT",EDGE,{"derivedFrom":sQuery(id+"F7.wireOp",EDGE,"E122.MirrorCS")}),1.0]])]});
            var Q2;
            Q2=makeQuery(id+"F7.imprint","IMPRINT",FACE,{"disambiguationData":[TD([[makeQuery(id+"F7.imprint","IMPRINT",EDGE,{"derivedFrom":sQuery(id+"F7.wireOp",EDGE,"E30.3.0")}),1.0]])]});
            var Q3;
            Q3=makeQuery(id+"F7.imprint","IMPRINT",FACE,{"disambiguationData":[TD([[makeQuery(id+"F7.imprint","IMPRINT",EDGE,{"derivedFrom":sQuery(id+"F7.wireOp",EDGE,"E37.MirrorCS")}),1.0]])]});
            var Q4;
            Q4=makeQuery(id+"F7.imprint","IMPRINT",FACE,{"disambiguationData":[TD([[makeQuery(id+"F7.imprint","IMPRINT",EDGE,{"derivedFrom":sQuery(id+"F7.wireOp",EDGE,"E43.MirrorCS")}),1.0]])]});
            var Q5;
            Q5=makeQuery(id+"F7.imprint","IMPRINT",FACE,{"disambiguationData":[TD([[makeQuery(id+"F7.imprint","IMPRINT",EDGE,{"derivedFrom":sQuery(id+"F7.wireOp",EDGE,"E49.MirrorCS")}),-1.0]])]});
            var Q6;
            Q6=makeQuery(id+"F7.imprint","IMPRINT",FACE,{"disambiguationData":[TD([[makeQuery(id+"F7.imprint","IMPRINT",EDGE,{"derivedFrom":sQuery(id+"F7.wireOp",EDGE,"E23.3.0")}),1.0]])]});
            var Q7;
            Q7=makeQuery(id+"F7.imprint","IMPRINT",FACE,{"disambiguationData":[TD([[makeQuery(id+"F7.imprint","IMPRINT",EDGE,{"derivedFrom":sQuery(id+"F7.wireOp",EDGE,"E30.2.0")}),1.0]])]});
            var Q8;
            Q8=makeQuery(id+"F7.imprint","IMPRINT",FACE,{"disambiguationData":[TD([[makeQuery(id+"F7.imprint","IMPRINT",EDGE,{"derivedFrom":sQuery(id+"F7.wireOp",EDGE,"E55.MirrorCS")}),1.0]])]});
            var Q9;
            Q9=makeQuery(id+"F7.imprint","IMPRINT",FACE,{"disambiguationData":[TD([[makeQuery(id+"F7.imprint","IMPRINT",EDGE,{"derivedFrom":sQuery(id+"F7.wireOp",EDGE,"E116.MirrorCS")}),1.0]])]});
            var Q10;
            Q10=makeQuery(id+"F7.imprint","IMPRINT",FACE,{"disambiguationData":[TD([[makeQuery(id+"F7.imprint","IMPRINT",EDGE,{"derivedFrom":sQuery(id+"F7.wireOp",EDGE,"E23.4.0")}),1.0]])]});
            var Q11;
            Q11=makeQuery(id+"F7.imprint","IMPRINT",FACE,{"disambiguationData":[TD([[makeQuery(id+"F7.imprint","IMPRINT",EDGE,{"derivedFrom":sQuery(id+"F7.wireOp",EDGE,"E23.2.0")}),1.0]])]});
            var Q12;
            Q12=makeQuery(id+"F7.imprint","IMPRINT",FACE,{"disambiguationData":[TD([[makeQuery(id+"F7.imprint","IMPRINT",EDGE,{"derivedFrom":sQuery(id+"F7.wireOp",EDGE,"E61.MirrorCS")}),1.0]])]});
            var Q13;
            {var subQ6=sQuery(id+"F7.wireOp",EDGE,"E128.MirrorCS");Q13=makeQuery(id+"F7.imprint","IMPRINT",FACE,{"disambiguationData":[TD([[makeQuery(id+"F7.imprint","IMPRINT",EDGE,{"derivedFrom":subQ6}),-1.0]])]});}
            var Q14;
            Q14=makeQuery(id+"F7.imprint","IMPRINT",FACE,{"disambiguationData":[TD([[makeQuery(id+"F7.imprint","IMPRINT",EDGE,{"derivedFrom":sQuery(id+"F7.wireOp",EDGE,"E30.1.0")}),1.0]])]});
            var Q15;
            {var subQ1=sQuery(id+"F7.wireOp",EDGE,"E8.2.6");Q15=makeQuery(id+"F7.imprint","IMPRINT",FACE,{"disambiguationData":[TD([[makeQuery(id+"F7.imprint","IMPRINT",EDGE,{"derivedFrom":subQ1}),-1.0]])]});}
            var Q16;
            {var subQ1=sQuery(id+"F7.wireOp",EDGE,"E8.5.6");Q16=makeQuery(id+"F7.imprint","IMPRINT",FACE,{"disambiguationData":[TD([[makeQuery(id+"F7.imprint","IMPRINT",EDGE,{"derivedFrom":subQ1}),-1.0]])]});}
            var Q17;
            {var subQ1=sQuery(id+"F7.wireOp",EDGE,"E8.4.6");Q17=makeQuery(id+"F7.imprint","IMPRINT",FACE,{"disambiguationData":[TD([[makeQuery(id+"F7.imprint","IMPRINT",EDGE,{"derivedFrom":subQ1}),-1.0]])]});}
            var Q18;
            {var subQ7=sQuery(id+"F7.wireOp",EDGE,"E8.3.6");Q18=makeQuery(id+"F7.imprint","IMPRINT",FACE,{"disambiguationData":[TD([[makeQuery(id+"F7.imprint","IMPRINT",EDGE,{"derivedFrom":subQ7}),-1.0]])]});}
            var Q19;
            {var subQ1=sQuery(id+"F7.wireOp",EDGE,"E6.1");Q19=makeQuery(id+"F7.imprint","IMPRINT",FACE,{"disambiguationData":[TD([[makeQuery(id+"F7.imprint","IMPRINT",EDGE,{"derivedFrom":subQ1}),-1.0]])]});}
            var Q20;
            {var subQ7=sQuery(id+"F7.wireOp",EDGE,"E8.1.6");Q20=makeQuery(id+"F7.imprint","IMPRINT",FACE,{"disambiguationData":[TD([[makeQuery(id+"F7.imprint","IMPRINT",EDGE,{"derivedFrom":subQ7}),-1.0]])]});}
            var Q21;
            Q21=makeQuery(id+"F7.imprint","IMPRINT",FACE,{"disambiguationData":[TD([[makeQuery(id+"F7.imprint","IMPRINT",EDGE,{"derivedFrom":sQuery(id+"F7.wireOp",EDGE,"E23.1.0")}),1.0]])]});
            var Q22;
            Q22=makeQuery(id+"F7.imprint","IMPRINT",FACE,{"disambiguationData":[TD([[makeQuery(id+"F7.imprint","IMPRINT",EDGE,{"derivedFrom":sQuery(id+"F7.wireOp",EDGE,"E67.MirrorCS")}),1.0]])]});
            var Q23;
            Q23=makeQuery(id+"F7.imprint","IMPRINT",FACE,{"disambiguationData":[TD([[makeQuery(id+"F7.imprint","IMPRINT",EDGE,{"derivedFrom":sQuery(id+"F7.wireOp",EDGE,"E23.5.0")}),1.0]])]});
            var Q24;
            Q24=makeQuery(id+"F7.imprint","IMPRINT",FACE,{"disambiguationData":[TD([[makeQuery(id+"F7.imprint","IMPRINT",EDGE,{"derivedFrom":sQuery(id+"F7.wireOp",EDGE,"E30.4.0")}),1.0]])]});
            var Q25;
            {var subQ5=sQuery(id+"F7.wireOp",EDGE,"E134.MirrorCS");Q25=makeQuery(id+"F7.imprint","IMPRINT",FACE,{"disambiguationData":[TD([[makeQuery(id+"F7.imprint","IMPRINT",EDGE,{"derivedFrom":subQ5}),-1.0]])]});}
            var Q26;
            Q26=makeQuery(id+"F7.imprint","IMPRINT",FACE,{"disambiguationData":[TD([[makeQuery(id+"F7.imprint","IMPRINT",EDGE,{"derivedFrom":sQuery(id+"F7.wireOp",EDGE,"E110.MirrorCS")}),1.0]])]});
            var Q27;
            Q27=makeQuery(id+"F7.imprint","IMPRINT",FACE,{"disambiguationData":[TD([[makeQuery(id+"F7.imprint","IMPRINT",EDGE,{"derivedFrom":sQuery(id+"F7.wireOp",EDGE,"E104.MirrorCS")}),1.0]])]});
            var Q28;
            Q28=makeQuery(id+"F7.imprint","IMPRINT",FACE,{"disambiguationData":[TD([[makeQuery(id+"F7.imprint","IMPRINT",EDGE,{"derivedFrom":sQuery(id+"F7.wireOp",EDGE,"E30.5.0")}),1.0]])]});
            var Q29;
            Q29=makeQuery(id+"F7.imprint","IMPRINT",FACE,{"disambiguationData":[TD([[makeQuery(id+"F7.imprint","IMPRINT",EDGE,{"derivedFrom":sQuery(id+"F7.wireOp",EDGE,"E17.MirrorCS")}),1.0]])]});
            var Q30;
            Q30=makeQuery(id+"F7.imprint","IMPRINT",FACE,{"disambiguationData":[TD([[makeQuery(id+"F7.imprint","IMPRINT",EDGE,{"derivedFrom":sQuery(id+"F7.wireOp",EDGE,"E24.MirrorCS")}),1.0]])]});
            var Q31;
            Q31=makeQuery(id+"F7.imprint","IMPRINT",FACE,{"disambiguationData":[TD([[makeQuery(id+"F7.imprint","IMPRINT",EDGE,{"derivedFrom":sQuery(id+"F7.wireOp",EDGE,"E73.MirrorCS")}),1.0]])]});
            var Q32;
            Q32=makeQuery(id+"F7.imprint","IMPRINT",FACE,{"disambiguationData":[TD([[makeQuery(id+"F7.imprint","IMPRINT",EDGE,{"derivedFrom":sQuery(id+"F7.wireOp",EDGE,"E79.MirrorCS")}),-1.0]])]});
            var Q33;
            Q33=makeQuery(id+"F7.imprint","IMPRINT",FACE,{"disambiguationData":[TD([[makeQuery(id+"F7.imprint","IMPRINT",EDGE,{"derivedFrom":sQuery(id+"F7.wireOp",EDGE,"E85.MirrorCS")}),1.0]])]});
            var Q34;
            Q34=makeQuery(id+"F7.imprint","IMPRINT",FACE,{"disambiguationData":[TD([[makeQuery(id+"F7.imprint","IMPRINT",EDGE,{"derivedFrom":sQuery(id+"F7.wireOp",EDGE,"E91.MirrorCS")}),1.0]])]});
            var Q35;
            Q35=makeQuery(id+"F7.imprint","IMPRINT",FACE,{"disambiguationData":[TD([[makeQuery(id+"F7.imprint","IMPRINT",EDGE,{"derivedFrom":sQuery(id+"F7.wireOp",EDGE,"E98.MirrorCS")}),-1.0]])]});
            extrude(context, id + "F8", {"entities" : qUnion([Q0, Q1, Q2, Q3, Q4, Q5, Q6, Q7, Q8, Q9, Q10, Q11, Q12, Q13, Q14, Q15, Q16, Q17, Q18, Q19, Q20, Q21, Q22, Q23, Q24, Q25, Q26, Q27, Q28, Q29, Q30, Q31, Q32, Q33, Q34, Q35]), "operationType" : NewBodyOperationType.REMOVE, "oppositeDirection" : true, "depth" : 25 * mm});
        }
    });
